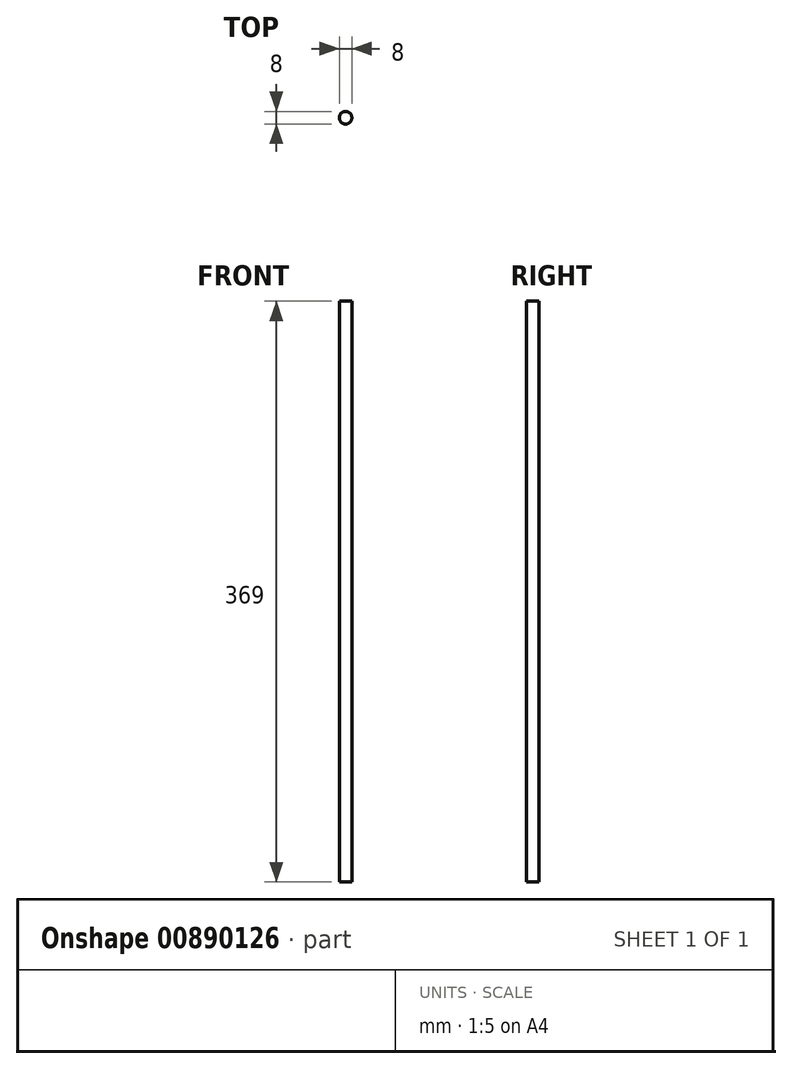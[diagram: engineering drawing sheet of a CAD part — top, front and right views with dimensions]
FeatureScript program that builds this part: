
annotation { "Feature Type Name" : "Feature", "Feature Type Description" : "" }
export const myFeature = defineFeature(function(context is Context, id is Id, definition is map)
    precondition{}
    {
        {
            var Q0;
            Q0=qCreatedBy(makeId("Top.planeOp"),FACE);
            var sketch = newSketch(context, id + "F0", { "sketchPlane" : qUnion([Q0])});
            skCircle(sketch, "E0", {"center": v(0, 0) * mm, "radius": 4 * mm});
            skSolve(sketch);
        }
        {
            var Q0;
            Q0=qSketchRegion(id+"F0",true);
            extrude(context, id + "F1", {"entities" : qUnion([Q0]), "depth" : 369 * mm, "offsetDistance" : 25 * mm});
        }
    });
